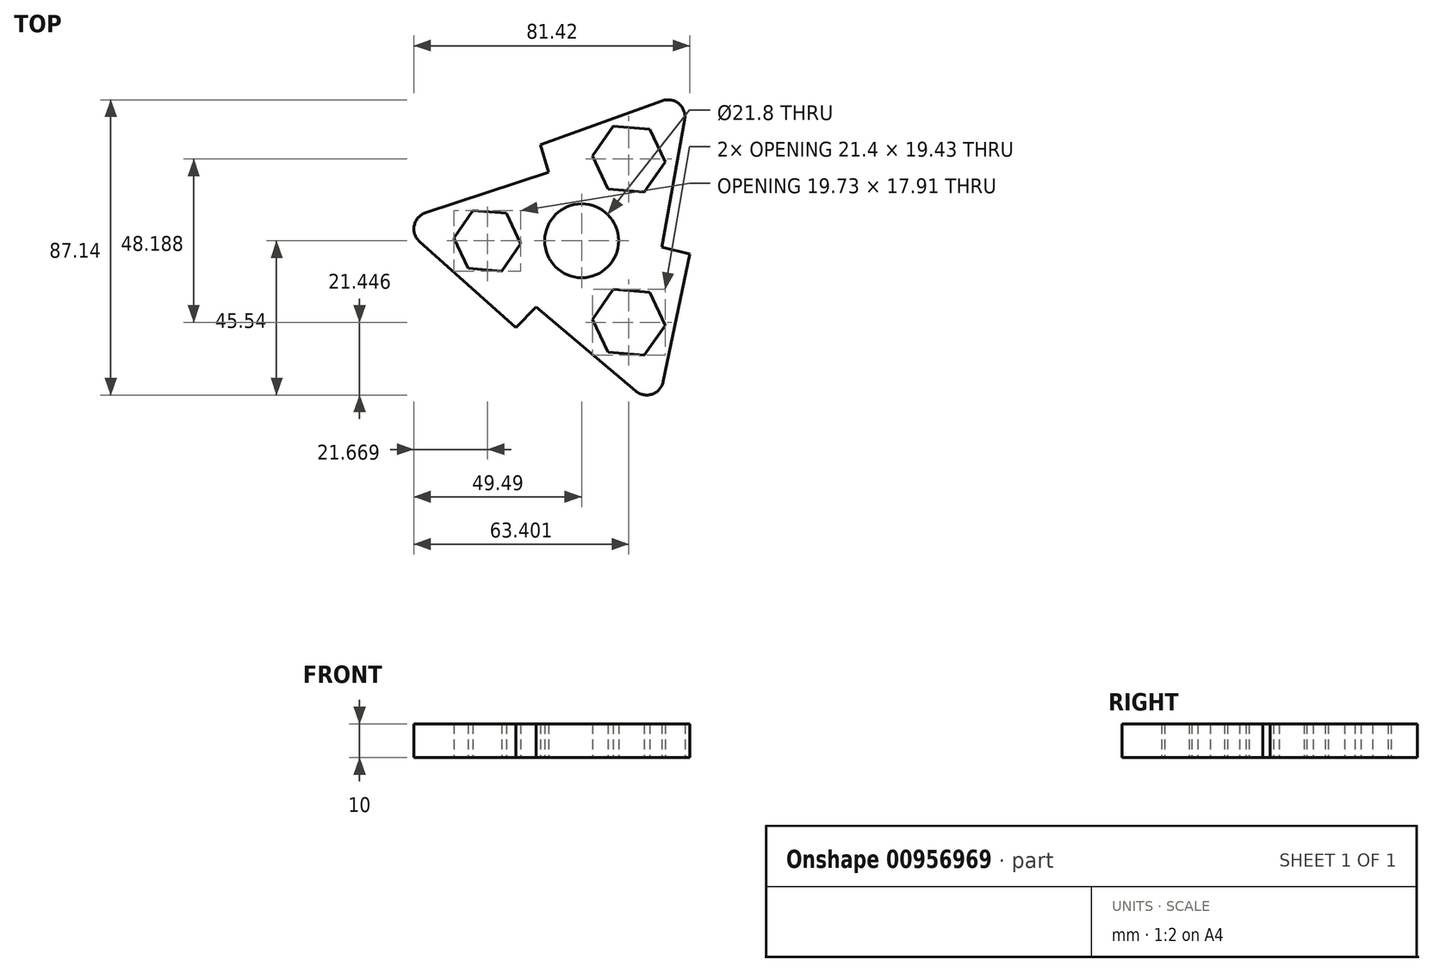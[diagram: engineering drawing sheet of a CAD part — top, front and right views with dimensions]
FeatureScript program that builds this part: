
annotation { "Feature Type Name" : "Feature", "Feature Type Description" : "" }
export const myFeature = defineFeature(function(context is Context, id is Id, definition is map)
    precondition{}
    {
        {
            var Q0;
            Q0=qCreatedBy(makeId("Top.planeOp"),FACE);
            var sketch = newSketch(context, id + "F0", { "sketchPlane" : qUnion([Q0])});
            skCircle(sketch, "E0", {"center": v(0, 0) * mm, "radius": 10.9 * mm});
            skCircle(sketch, "E1.cCircle", {"center": v(-27.82, 0) * mm, "radius": 8.57 * mm, "construction": true});
            skLineSegment(sketch, "E1.0", {"start": v(-37.69, 0.82) * mm, "end": v(-32.04, 8.96) * mm});
            skLineSegment(sketch, "E1.1", {"start": v(-32.04, 8.96) * mm, "end": v(-22.17, 8.13) * mm});
            skLineSegment(sketch, "E1.2", {"start": v(-22.17, 8.13) * mm, "end": v(-17.95, -0.82) * mm});
            skLineSegment(sketch, "E1.3", {"start": v(-17.95, -0.82) * mm, "end": v(-23.6, -8.96) * mm});
            skLineSegment(sketch, "E1.4", {"start": v(-23.6, -8.96) * mm, "end": v(-33.47, -8.13) * mm});
            skLineSegment(sketch, "E1.5", {"start": v(-33.47, -8.13) * mm, "end": v(-37.69, 0.82) * mm});
            skPoint(sketch, "E1.0.midPoint", {"position": v(-34.86, 4.9) * mm});
            skCircle(sketch, "E2.cCircle", {"center": v(-27.82, 0) * mm, "radius": 13.51 * mm, "construction": true});
            skLineSegment(sketch, "E2.0", {"start": v(-54.28, 5.53) * mm, "end": v(-9.8, 20.15) * mm});
            skLineSegment(sketch, "E2.2", {"start": v(-19.38, -25.68) * mm, "end": v(-54.28, 5.53) * mm});
            skPoint(sketch, "E2.0.midPoint", {"position": v(-32.04, 12.84) * mm});
            skLineSegment(sketch, "E3.1.1", {"start": v(31.93, -3.95) * mm, "end": v(22.35, -49.77) * mm});
            skLineSegment(sketch, "E3.1.2", {"start": v(22.35, -49.77) * mm, "end": v(-13.4, -19.55) * mm});
            skCircle(sketch, "E3.1.3", {"center": v(13.91, -24.1) * mm, "radius": 13.51 * mm, "construction": true});
            skLineSegment(sketch, "E3.1.4", {"start": v(18.49, -33.8) * mm, "end": v(7.79, -32.91) * mm});
            skLineSegment(sketch, "E3.1.5", {"start": v(24.61, -24.99) * mm, "end": v(18.49, -33.8) * mm});
            skCircle(sketch, "E3.1.6", {"center": v(13.91, -24.1) * mm, "radius": 9.3 * mm, "construction": true});
            skLineSegment(sketch, "E3.1.7", {"start": v(20.04, -15.27) * mm, "end": v(24.61, -24.99) * mm});
            skLineSegment(sketch, "E3.1.8", {"start": v(9.33, -14.38) * mm, "end": v(20.04, -15.27) * mm});
            skLineSegment(sketch, "E3.1.9", {"start": v(7.79, -32.91) * mm, "end": v(3.2, -23.2) * mm});
            skLineSegment(sketch, "E3.1.10", {"start": v(3.2, -23.2) * mm, "end": v(9.33, -14.38) * mm});
            skLineSegment(sketch, "E3.2.1", {"start": v(-12.12, 28.39) * mm, "end": v(31.93, 44.24) * mm});
            skLineSegment(sketch, "E3.2.2", {"start": v(31.93, 44.24) * mm, "end": v(23.63, -1.83) * mm});
            skCircle(sketch, "E3.2.3", {"center": v(13.91, 24.1) * mm, "radius": 13.51 * mm, "construction": true});
            skLineSegment(sketch, "E3.2.4", {"start": v(20.04, 32.91) * mm, "end": v(24.61, 23.2) * mm});
            skLineSegment(sketch, "E3.2.5", {"start": v(9.33, 33.8) * mm, "end": v(20.04, 32.91) * mm});
            skCircle(sketch, "E3.2.6", {"center": v(13.91, 24.1) * mm, "radius": 9.3 * mm, "construction": true});
            skLineSegment(sketch, "E3.2.7", {"start": v(3.2, 24.99) * mm, "end": v(9.33, 33.8) * mm});
            skLineSegment(sketch, "E3.2.8", {"start": v(7.79, 15.27) * mm, "end": v(3.2, 24.99) * mm});
            skLineSegment(sketch, "E3.2.9", {"start": v(24.61, 23.2) * mm, "end": v(18.49, 14.38) * mm});
            skLineSegment(sketch, "E3.2.10", {"start": v(18.49, 14.38) * mm, "end": v(7.79, 15.27) * mm});
            skLineSegment(sketch, "E4", {"start": v(-19.38, -25.68) * mm, "end": v(-13.4, -19.55) * mm});
            skLineSegment(sketch, "E5", {"start": v(-9.8, 20.15) * mm, "end": v(-12.12, 28.39) * mm});
            skLineSegment(sketch, "E6", {"start": v(23.63, -1.83) * mm, "end": v(31.93, -3.95) * mm});
            skSolve(sketch);
        }
        {
            var Q0;
            Q0 = qSketchRegion(id + "F0", true);
            extrude(context, id + "F1", {"entities" : qUnion([Q0]), "depth" : 10 * mm, "offsetDistance" : 25 * mm});
        }
        {
            var Q0;
            Q0=makeQuery(id+"F1.opExtrude","SWEPT_EDGE",EDGE,{"disambiguationData":[OSD([sQuery(id+"F0.wireOp",EDGE,"E3.1.1"),sQuery(id+"F0.wireOp",EDGE,"E3.1.2")])]});
            var Q1;
            Q1=makeQuery(id+"F1.opExtrude","SWEPT_EDGE",EDGE,{"disambiguationData":[OSD([sQuery(id+"F0.wireOp",EDGE,"E3.2.1"),sQuery(id+"F0.wireOp",EDGE,"E3.2.2")])]});
            var Q2;
            Q2=makeQuery(id+"F1.opExtrude","SWEPT_EDGE",EDGE,{"disambiguationData":[OSD([sQuery(id+"F0.wireOp",EDGE,"E2.0"),sQuery(id+"F0.wireOp",EDGE,"E2.2")])]});
            fillet(context, id + "F2", {"entities" : qUnion([Q0, Q1, Q2]), "radius" : 5 * mm, "tangentPropagation" : true, "allowEdgeOverflow" : false});
        }
    });
